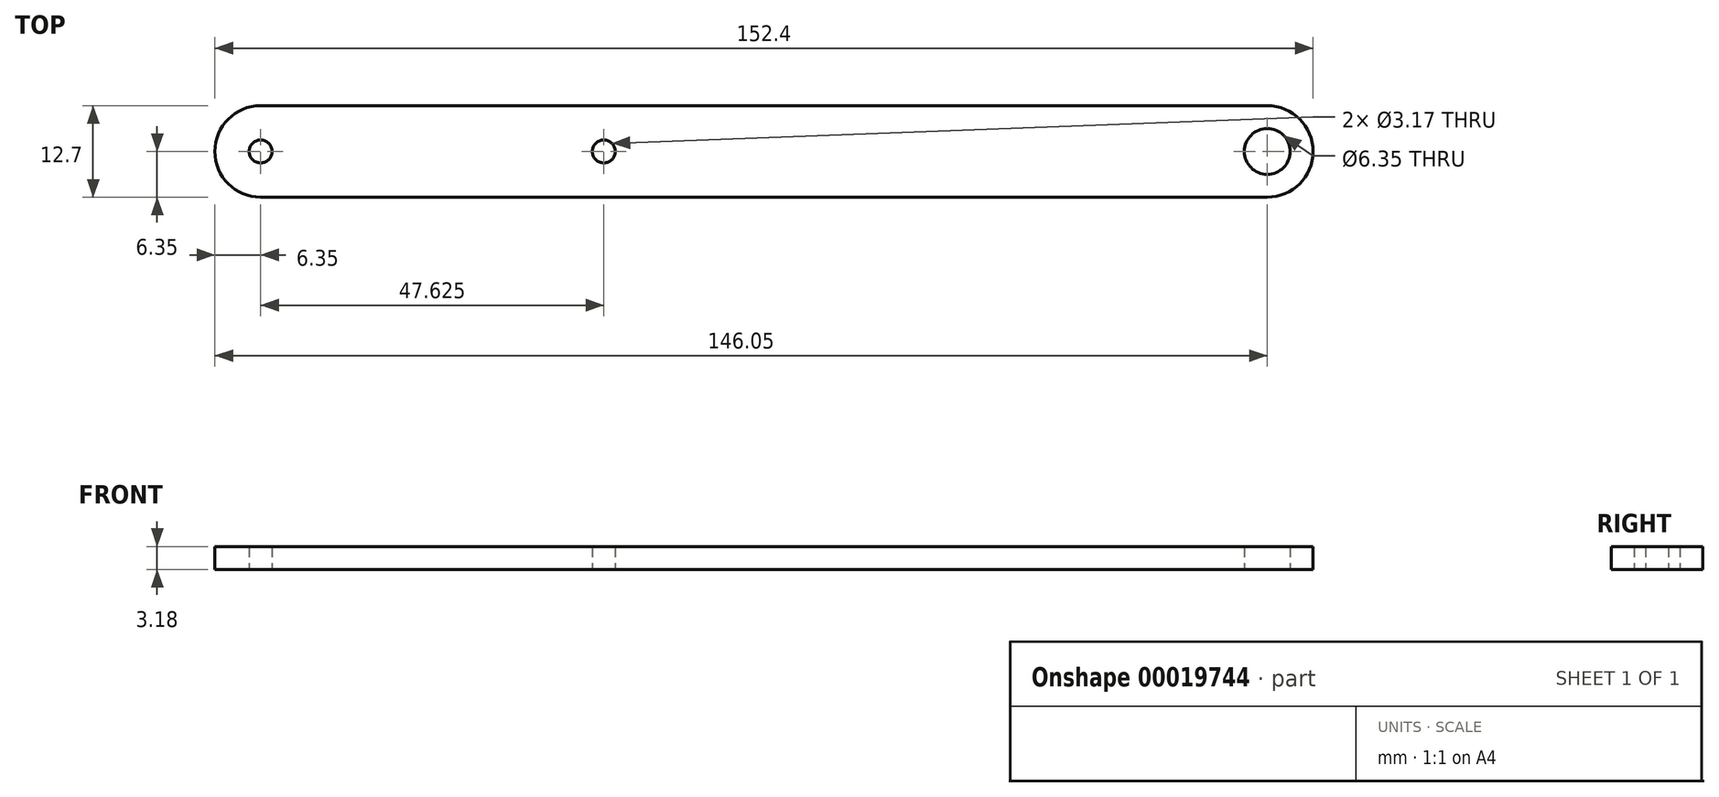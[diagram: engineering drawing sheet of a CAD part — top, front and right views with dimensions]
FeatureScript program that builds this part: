
annotation { "Feature Type Name" : "Feature", "Feature Type Description" : "" }
export const myFeature = defineFeature(function(context is Context, id is Id, definition is map)
    precondition{}
    {
        {
            var Q0;
            Q0=qCreatedBy(makeId("Top.planeOp"),FACE);
            var sketch = newSketch(context, id + "F0", { "sketchPlane" : qUnion([Q0])});
            skLineSegment(sketch, "E0", {"start": v(0, 0) * mm, "end": v(139.7, 0) * mm});
            skArc(sketch, "E1", {"start": v(139.7, 0) * mm, "mid": v(146.05, 6.35) * mm, "end": v(139.7, 12.7) * mm});
            skLineSegment(sketch, "E2", {"start": v(139.7, 12.7) * mm, "end": v(0, 12.7) * mm});
            skArc(sketch, "E3", {"start": v(0, 12.7) * mm, "mid": v(-6.35, 6.35) * mm, "end": v(0, 0) * mm});
            skCircle(sketch, "E4", {"center": v(0, 6.35) * mm, "radius": 1.59 * mm});
            skCircle(sketch, "E5", {"center": v(47.63, 6.35) * mm, "radius": 1.59 * mm});
            skCircle(sketch, "E6", {"center": v(139.7, 6.35) * mm, "radius": 3.18 * mm});
            skSolve(sketch);
        }
        {
            var Q0;
            Q0 = qSketchRegion(id + "F0", true);
            extrude(context, id + "F1", {"entities" : qUnion([Q0]), "depth" : 3.17 * mm});
        }
    });
